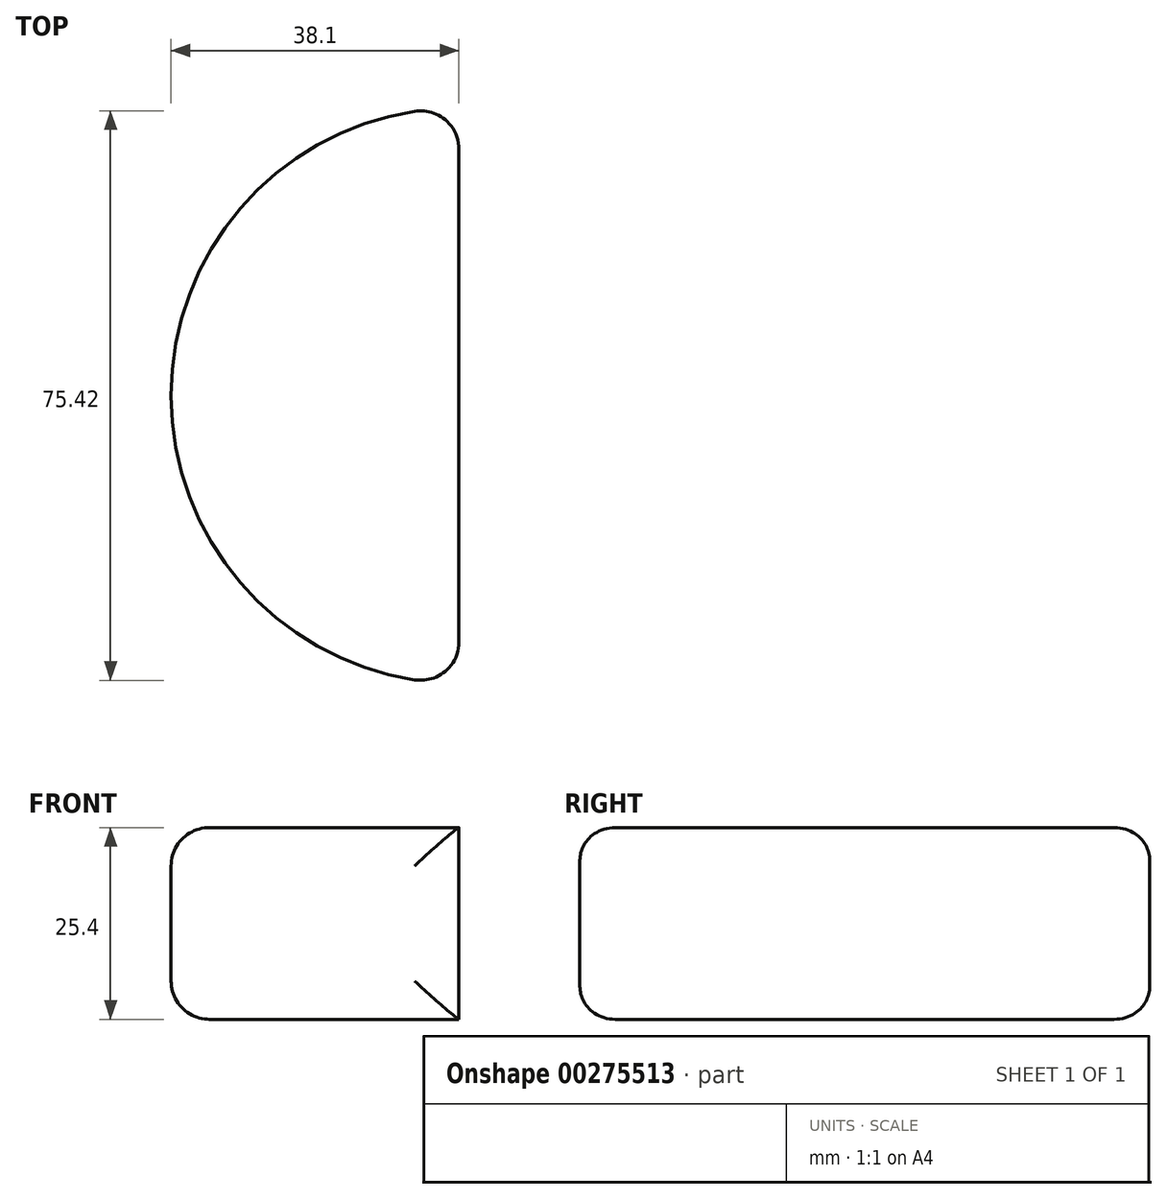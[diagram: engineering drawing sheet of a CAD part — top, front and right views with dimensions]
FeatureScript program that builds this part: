
annotation { "Feature Type Name" : "Feature", "Feature Type Description" : "" }
export const myFeature = defineFeature(function(context is Context, id is Id, definition is map)
    precondition{}
    {
        {
            var Q0;
            Q0=qCreatedBy(makeId("Top.planeOp"),FACE);
            var sketch = newSketch(context, id + "F0", { "sketchPlane" : qUnion([Q0])});
            skCircle(sketch, "E0", {"center": v(0, 0) * mm, "radius": 38.1 * mm});
            skSolve(sketch);
        }
        {
            var Q0;
            Q0 = qSketchRegion(id + "F0", true);
            extrude(context, id + "F1", {"entities" : qUnion([Q0]), "depth" : 25.4 * mm});
        }
        {
            var Q0;
            Q0=makeQuery(id+"F1.opExtrude","CAP_FACE",FACE,{"disambiguationData":[OSD([sQuery(id+"F0.wireOp",EDGE,"E0")])],"isStart":false});
            var sketch = newSketch(context, id + "F2", { "sketchPlane" : qUnion([Q0])});
            skLineSegment(sketch, "E1.bottom", {"start": v(0, 40.87) * mm, "end": v(44.03, 40.87) * mm});
            skLineSegment(sketch, "E1.top", {"start": v(0, -44.6) * mm, "end": v(44.03, -44.6) * mm});
            skLineSegment(sketch, "E1.left", {"start": v(0, 40.87) * mm, "end": v(0, -44.6) * mm});
            skLineSegment(sketch, "E1.right", {"start": v(44.03, 40.87) * mm, "end": v(44.03, -44.6) * mm});
            skSolve(sketch);
        }
        {
            var Q0;
            Q0 = qSketchRegion(id + "F2", true);
            extrude(context, id + "F3", {"entities" : qUnion([Q0]), "operationType" : NewBodyOperationType.REMOVE, "oppositeDirection" : true, "depth" : 25.4 * mm});
        }
        {
            var Q0;
            Q0=makeQuery(id+"F3.boolean.opBoolean","COPY",EDGE,{"derivedFrom":makeQuery(id+"F3.opExtrude","CAP_EDGE",EDGE,{"disambiguationData":[OSD([sQuery(id+"F2.wireOp",EDGE,"E1.left")])],"isStart":true})});
            var Q1;
            Q1=makeQuery(id+"F3.boolean.opBoolean","INTERSECT",EDGE,{"disambiguationData":[OD(0.0)],"derivedFrom":[makeQuery(id+"F1.opExtrude","SWEPT_FACE",FACE,{"disambiguationData":[OSD([sQuery(id+"F0.wireOp",EDGE,"E0")])]}),makeQuery(id+"F3.opExtrude","SWEPT_FACE",FACE,{"disambiguationData":[OSD([sQuery(id+"F2.wireOp",EDGE,"E1.left")])]})]});
            var Q2;
            Q2=makeQuery(id+"F1.opExtrude","CAP_EDGE",EDGE,{"disambiguationData":[OSD([sQuery(id+"F0.wireOp",EDGE,"E0")])],"isStart":false});
            var Q3;
            Q3=makeQuery(id+"F1.opExtrude","CAP_EDGE",EDGE,{"disambiguationData":[OSD([sQuery(id+"F0.wireOp",EDGE,"E0")])],"isStart":true});
            var Q4;
            Q4=makeQuery(id+"F3.boolean.opBoolean","COPY",EDGE,{"derivedFrom":makeQuery(id+"F3.opExtrude","CAP_EDGE",EDGE,{"disambiguationData":[OSD([sQuery(id+"F2.wireOp",EDGE,"E1.left")])],"isStart":false})});
            var Q5;
            Q5=makeQuery(id+"F3.boolean.opBoolean","INTERSECT",EDGE,{"disambiguationData":[OD(1.0)],"derivedFrom":[makeQuery(id+"F1.opExtrude","SWEPT_FACE",FACE,{"disambiguationData":[OSD([sQuery(id+"F0.wireOp",EDGE,"E0")])]}),makeQuery(id+"F3.opExtrude","SWEPT_FACE",FACE,{"disambiguationData":[OSD([sQuery(id+"F2.wireOp",EDGE,"E1.left")])]})]});
            fillet(context, id + "F4", {"entities" : qUnion([Q0, Q1, Q2, Q3, Q4, Q5]), "radius" : 5.08 * mm, "tangentPropagation" : true, "allowEdgeOverflow" : false});
        }
    });
